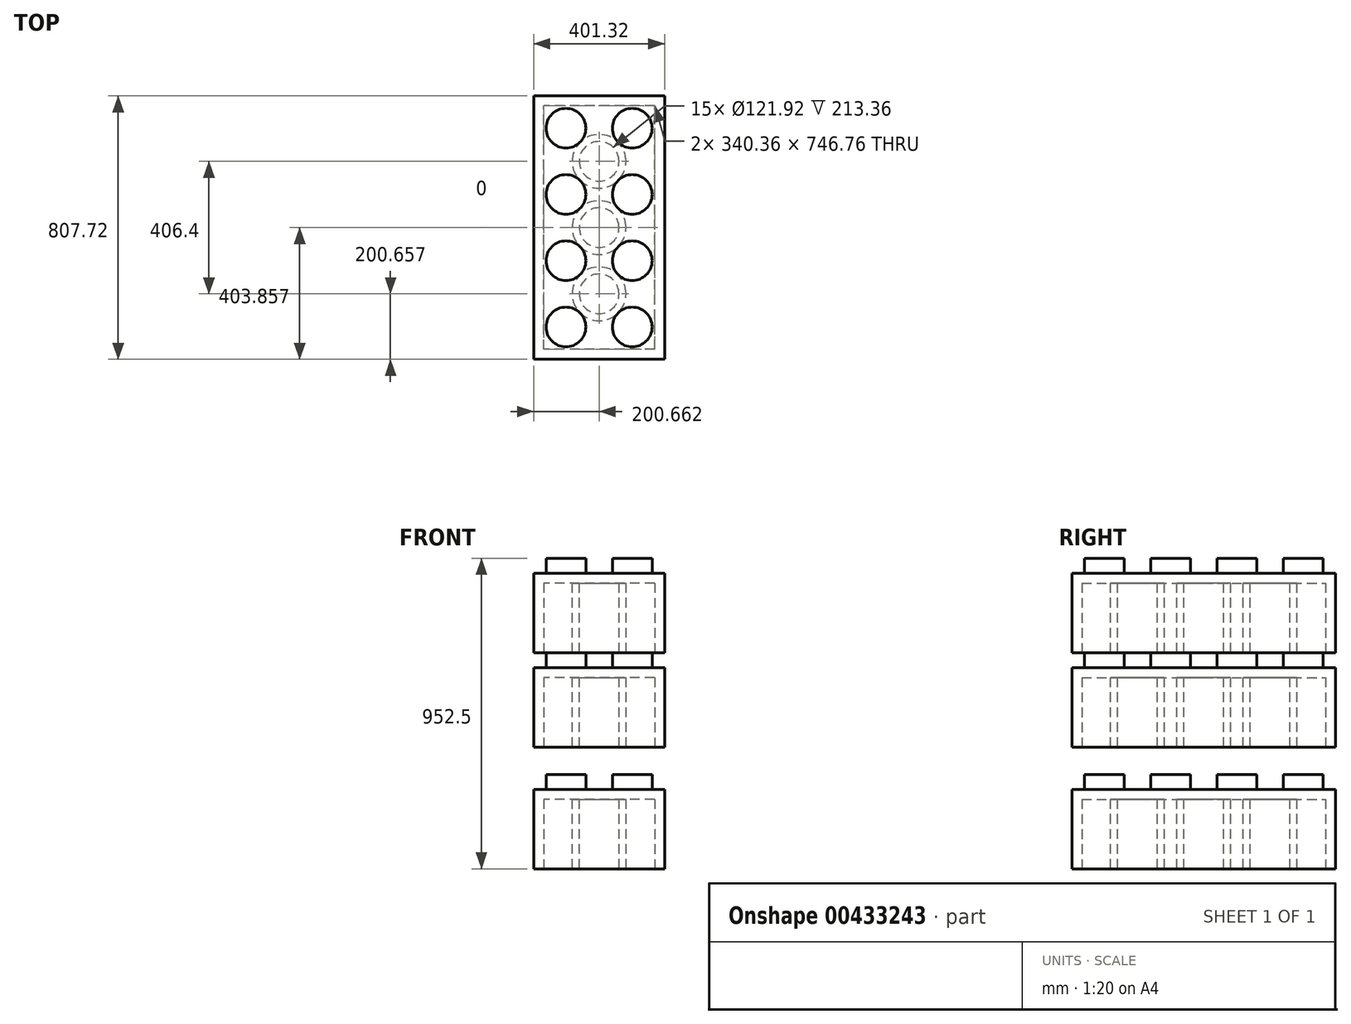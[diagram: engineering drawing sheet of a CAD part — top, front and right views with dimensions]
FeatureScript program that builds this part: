
annotation { "Feature Type Name" : "Feature", "Feature Type Description" : "" }
export const myFeature = defineFeature(function(context is Context, id is Id, definition is map)
    precondition{}
    {
        {
            var Q0;
            Q0=qCreatedBy(makeId("Top.planeOp"),FACE);
            var sketch = newSketch(context, id + "F0", { "sketchPlane" : qUnion([Q0])});
            skLineSegment(sketch, "E0.bottom", {"start": v(-238.99, -404.33) * mm, "end": v(162.33, -404.33) * mm});
            skLineSegment(sketch, "E0.top", {"start": v(-238.99, 403.39) * mm, "end": v(162.33, 403.39) * mm});
            skLineSegment(sketch, "E0.left", {"start": v(-238.99, -404.33) * mm, "end": v(-238.99, 403.39) * mm});
            skLineSegment(sketch, "E0.right", {"start": v(162.33, -404.33) * mm, "end": v(162.33, 403.39) * mm});
            skSolve(sketch);
        }
        {
            var Q0;
            Q0=makeQuery(id+"F0.imprint","IMPRINT",FACE,{"disambiguationData":[TD([[makeQuery(id+"F0.imprint","IMPRINT",EDGE,{"derivedFrom":sQuery(id+"F0.wireOp",EDGE,"E0.bottom")}),1.0]])]});
            extrude(context, id + "F1", {"entities" : qUnion([Q0]), "depth" : 243.84 * mm});
        }
        {
            var Q0;
            Q0=makeQuery(id+"F1.opExtrude","CAP_FACE",FACE,{"disambiguationData":[OSD([sQuery(id+"F0.wireOp",EDGE,"E0.bottom"),sQuery(id+"F0.wireOp",EDGE,"E0.top"),sQuery(id+"F0.wireOp",EDGE,"E0.left"),sQuery(id+"F0.wireOp",EDGE,"E0.right")])],"isStart":false});
            var sketch = newSketch(context, id + "F2", { "sketchPlane" : qUnion([Q0])});
            skCircle(sketch, "E1", {"center": v(63.27, -305.27) * mm, "radius": 60.96 * mm});
            skCircle(sketch, "E2.0.1.0", {"center": v(63.27, -102.07) * mm, "radius": 60.96 * mm});
            skCircle(sketch, "E2.0.2.0", {"center": v(63.27, 101.13) * mm, "radius": 60.96 * mm});
            skCircle(sketch, "E2.0.3.0", {"center": v(63.27, 304.33) * mm, "radius": 60.96 * mm});
            skCircle(sketch, "E2.1.0.0", {"center": v(-139.93, -305.27) * mm, "radius": 60.96 * mm});
            skCircle(sketch, "E2.1.1.0", {"center": v(-139.93, -102.07) * mm, "radius": 60.96 * mm});
            skCircle(sketch, "E2.1.2.0", {"center": v(-139.93, 101.13) * mm, "radius": 60.96 * mm});
            skCircle(sketch, "E2.1.3.0", {"center": v(-139.93, 304.33) * mm, "radius": 60.96 * mm});
            skLineSegment(sketch, "E2.direction1", {"start": v(63.27, -305.27) * mm, "end": v(-139.93, -305.27) * mm, "construction": true});
            skLineSegment(sketch, "E2.direction2", {"start": v(63.27, -305.27) * mm, "end": v(63.27, -102.07) * mm, "construction": true});
            skSolve(sketch);
        }
        {
            var Q0;
            Q0=makeQuery(id+"F2.imprint","IMPRINT",FACE,{"disambiguationData":[TD([[makeQuery(id+"F2.imprint","IMPRINT",EDGE,{"derivedFrom":sQuery(id+"F2.wireOp",EDGE,"E2.1.0.0")}),1.0]])]});
            var Q1;
            Q1=makeQuery(id+"F2.imprint","IMPRINT",FACE,{"disambiguationData":[TD([[makeQuery(id+"F2.imprint","IMPRINT",EDGE,{"derivedFrom":sQuery(id+"F2.wireOp",EDGE,"E2.1.1.0")}),1.0]])]});
            var Q2;
            Q2=makeQuery(id+"F2.imprint","IMPRINT",FACE,{"disambiguationData":[TD([[makeQuery(id+"F2.imprint","IMPRINT",EDGE,{"derivedFrom":sQuery(id+"F2.wireOp",EDGE,"E2.1.2.0")}),1.0]])]});
            var Q3;
            Q3=makeQuery(id+"F2.imprint","IMPRINT",FACE,{"disambiguationData":[TD([[makeQuery(id+"F2.imprint","IMPRINT",EDGE,{"derivedFrom":sQuery(id+"F2.wireOp",EDGE,"E2.1.3.0")}),1.0]])]});
            var Q4;
            Q4=makeQuery(id+"F2.imprint","IMPRINT",FACE,{"disambiguationData":[TD([[makeQuery(id+"F2.imprint","IMPRINT",EDGE,{"derivedFrom":sQuery(id+"F2.wireOp",EDGE,"E2.0.3.0")}),1.0]])]});
            var Q5;
            Q5=makeQuery(id+"F2.imprint","IMPRINT",FACE,{"disambiguationData":[TD([[makeQuery(id+"F2.imprint","IMPRINT",EDGE,{"derivedFrom":sQuery(id+"F2.wireOp",EDGE,"E2.0.2.0")}),1.0]])]});
            var Q6;
            Q6=makeQuery(id+"F2.imprint","IMPRINT",FACE,{"disambiguationData":[TD([[makeQuery(id+"F2.imprint","IMPRINT",EDGE,{"derivedFrom":sQuery(id+"F2.wireOp",EDGE,"E2.0.1.0")}),1.0]])]});
            var Q7;
            Q7=makeQuery(id+"F2.imprint","IMPRINT",FACE,{"disambiguationData":[TD([[makeQuery(id+"F2.imprint","IMPRINT",EDGE,{"derivedFrom":sQuery(id+"F2.wireOp",EDGE,"E1")}),1.0]])]});
            extrude(context, id + "F3", {"entities" : qUnion([Q0, Q1, Q2, Q3, Q4, Q5, Q6, Q7]), "operationType" : NewBodyOperationType.ADD, "depth" : 45.72 * mm});
        }
        {
            var Q0;
            Q0=makeQuery(id+"F1.opExtrude","CAP_FACE",FACE,{"disambiguationData":[OSD([sQuery(id+"F0.wireOp",EDGE,"E0.bottom"),sQuery(id+"F0.wireOp",EDGE,"E0.top"),sQuery(id+"F0.wireOp",EDGE,"E0.left"),sQuery(id+"F0.wireOp",EDGE,"E0.right")])],"isStart":true});
            var sketch = newSketch(context, id + "F4", { "sketchPlane" : qUnion([Q0])});
            skLineSegment(sketch, "E3.bottom", {"start": v(131.85, 373.85) * mm, "end": v(-208.5, 373.85) * mm});
            skLineSegment(sketch, "E3.top", {"start": v(131.85, -372.9) * mm, "end": v(-208.5, -372.9) * mm});
            skLineSegment(sketch, "E3.left", {"start": v(131.85, 373.85) * mm, "end": v(131.85, -372.9) * mm});
            skLineSegment(sketch, "E3.right", {"start": v(-208.5, 373.85) * mm, "end": v(-208.5, -372.9) * mm});
            skSolve(sketch);
        }
        {
            var Q0;
            Q0=makeQuery(id+"F4.imprint","IMPRINT",FACE,{"disambiguationData":[TD([[makeQuery(id+"F4.imprint","IMPRINT",EDGE,{"derivedFrom":sQuery(id+"F4.wireOp",EDGE,"E3.bottom")}),1.0]])]});
            extrude(context, id + "F5", {"entities" : qUnion([Q0]), "operationType" : NewBodyOperationType.REMOVE, "oppositeDirection" : true, "depth" : 213.36 * mm});
        }
        {
            var Q0;
            Q0=makeQuery(id+"F5.boolean.opBoolean","COPY",FACE,{"derivedFrom":makeQuery(id+"F5.opExtrude","CAP_FACE",FACE,{"disambiguationData":[OSD([sQuery(id+"F4.wireOp",EDGE,"E3.bottom"),sQuery(id+"F4.wireOp",EDGE,"E3.top"),sQuery(id+"F4.wireOp",EDGE,"E3.left"),sQuery(id+"F4.wireOp",EDGE,"E3.right")])],"isStart":false})});
            var sketch = newSketch(context, id + "F6", { "sketchPlane" : qUnion([Q0])});
            skCircle(sketch, "E4", {"center": v(-38.33, 203.67) * mm, "radius": 82.55 * mm});
            skCircle(sketch, "E5", {"center": v(-38.33, 203.67) * mm, "radius": 60.96 * mm});
            skCircle(sketch, "E6.0.1.0", {"center": v(-38.33, 0.47) * mm, "radius": 82.55 * mm});
            skCircle(sketch, "E6.0.1.1", {"center": v(-38.33, 0.47) * mm, "radius": 60.96 * mm});
            skCircle(sketch, "E6.0.2.0", {"center": v(-38.33, -202.73) * mm, "radius": 82.55 * mm});
            skCircle(sketch, "E6.0.2.1", {"center": v(-38.33, -202.73) * mm, "radius": 60.96 * mm});
            skLineSegment(sketch, "E6.direction1", {"start": v(-38.33, 203.67) * mm, "end": v(-12.93, 203.67) * mm, "construction": true});
            skLineSegment(sketch, "E6.direction2", {"start": v(-38.33, 203.67) * mm, "end": v(-38.33, 0.47) * mm, "construction": true});
            skSolve(sketch);
        }
        {
            var Q0;
            Q0=makeQuery(id+"F6.imprint","IMPRINT",FACE,{"disambiguationData":[TD([[makeQuery(id+"F6.imprint","IMPRINT",EDGE,{"derivedFrom":sQuery(id+"F6.wireOp",EDGE,"E4")}),1.0]])]});
            var Q1;
            Q1=makeQuery(id+"F6.imprint","IMPRINT",FACE,{"disambiguationData":[TD([[makeQuery(id+"F6.imprint","IMPRINT",EDGE,{"derivedFrom":sQuery(id+"F6.wireOp",EDGE,"E6.0.1.0")}),1.0]])]});
            var Q2;
            Q2=makeQuery(id+"F6.imprint","IMPRINT",FACE,{"disambiguationData":[TD([[makeQuery(id+"F6.imprint","IMPRINT",EDGE,{"derivedFrom":sQuery(id+"F6.wireOp",EDGE,"E6.0.2.0")}),1.0]])]});
            extrude(context, id + "F7", {"entities" : qUnion([Q0, Q1, Q2]), "operationType" : NewBodyOperationType.ADD, "depth" : 213.36 * mm});
        }
        {
            var Q0;
            Q0=makeQuery(id+"F1.opExtrude","SWEPT_BODY",BODY,{"disambiguationData":[OSD([sQuery(id+"F0.wireOp",EDGE,"E0.bottom"),sQuery(id+"F0.wireOp",EDGE,"E0.top"),sQuery(id+"F0.wireOp",EDGE,"E0.left"),sQuery(id+"F0.wireOp",EDGE,"E0.right")])]});
            transform(context, id + "F8", {"entities" : qUnion([Q0]), "transformType" : TransformType.TRANSLATION_3D, "dx" : 0 * mm, "dy" : 0 * mm, "dz" : 373.38 * mm, "makeCopy" : true});
        }
        {
            var Q0;
            Q0=makeQuery(id+"F8.opPattern","COPY",BODY,{"derivedFrom":makeQuery(id+"F1.opExtrude","SWEPT_BODY",BODY,{"disambiguationData":[OSD([sQuery(id+"F0.wireOp",EDGE,"E0.bottom"),sQuery(id+"F0.wireOp",EDGE,"E0.top"),sQuery(id+"F0.wireOp",EDGE,"E0.left"),sQuery(id+"F0.wireOp",EDGE,"E0.right")])]}),"instanceName":"1"});
            transform(context, id + "F9", {"entities" : qUnion([Q0]), "transformType" : TransformType.TRANSLATION_3D, "dx" : 0 * mm, "dy" : 0 * mm, "dz" : 289.56 * mm, "makeCopy" : true});
        }
        {
            var Q0;
            Q0=makeQuery(id+"F1.opExtrude","SWEPT_BODY",BODY,{"disambiguationData":[OSD([sQuery(id+"F0.wireOp",EDGE,"E0.bottom"),sQuery(id+"F0.wireOp",EDGE,"E0.top"),sQuery(id+"F0.wireOp",EDGE,"E0.left"),sQuery(id+"F0.wireOp",EDGE,"E0.right")])]});
            transform(context, id + "F10", {"entities" : qUnion([Q0]), "transformType" : TransformType.TRANSLATION_3D, "dx" : 0 * mm, "dy" : 0 * mm, "dz" : 0 * mm, "makeCopy" : true});
        }
        {
            var Q0;
            Q0=makeQuery(id+"F10.opPattern","COPY",BODY,{"derivedFrom":makeQuery(id+"F1.opExtrude","SWEPT_BODY",BODY,{"disambiguationData":[OSD([sQuery(id+"F0.wireOp",EDGE,"E0.bottom"),sQuery(id+"F0.wireOp",EDGE,"E0.top"),sQuery(id+"F0.wireOp",EDGE,"E0.left"),sQuery(id+"F0.wireOp",EDGE,"E0.right")])]}),"instanceName":"1"});
            transform(context, id + "F11", {"entities" : qUnion([Q0]), "transformType" : TransformType.TRANSLATION_3D, "dx" : 0 * mm, "dy" : 0 * mm, "dz" : 0 * mm, "makeCopy" : true});
        }
    });
